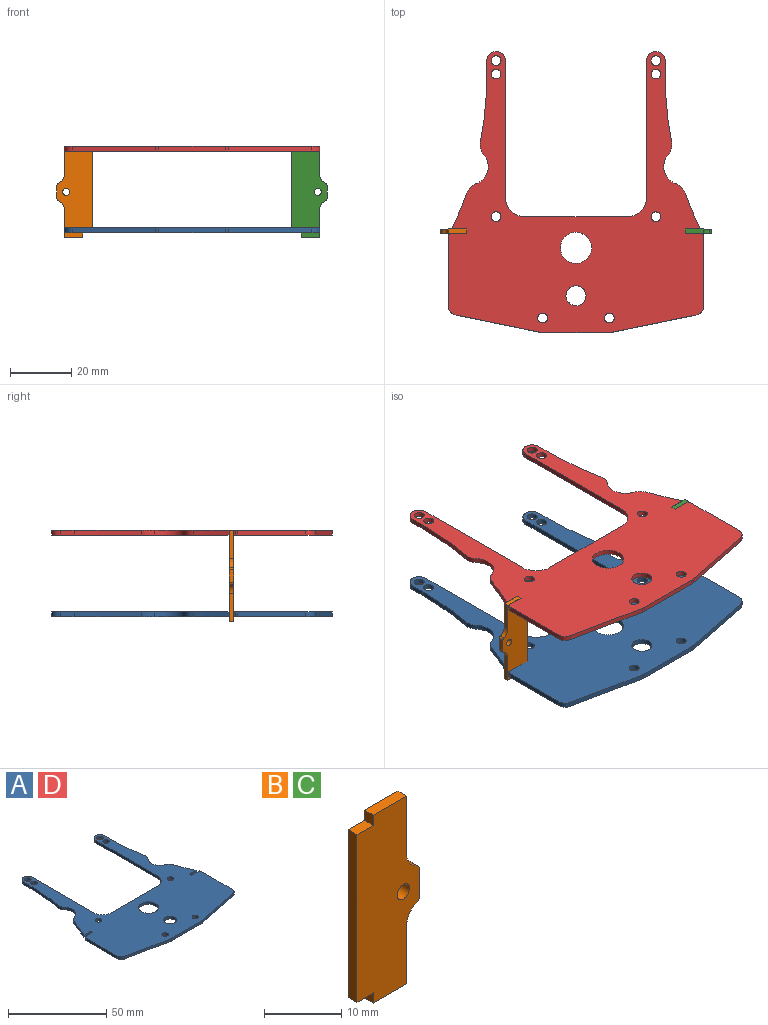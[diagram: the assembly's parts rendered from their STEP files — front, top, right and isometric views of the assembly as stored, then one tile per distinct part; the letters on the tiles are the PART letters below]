
ASSEMBLY  parts=4 mates=3
PART A: 55 faces, bbox 83.2x91.5x1.6 mm
  f0: cylinder r=116.85mm len=11.6mm, axis (0,0,-1), area 19.7mm2, adj f1,f6,f47,f52
  f1: plane 91.49x83.18mm, normal (0,0,-1), area 3595.5mm2, adj f0,f2,f3,f4,f5,f7,f8,f9
  f2: cylinder r=116.85mm len=1.57mm, axis (0,0,-1), area 0.7mm2, adj f1,f6,f20,f49
  f3: cylinder r=116.85mm len=1.57mm, axis (0,0,-1), area 0.7mm2, adj f1,f6,f10,f53
  f4: cylinder r=116.85mm len=22mm, axis (0,0,-1), area 34.7mm2, adj f1,f6,f9,f48
  f5: cylinder r=116.85mm len=22mm, axis (0,0,-1), area 34.7mm2, adj f1,f6,f22,f45
  f6: plane 91.49x83.18mm, normal (0,0,1), area 3595.5mm2, adj f0,f2,f3,f4,f5,f7,f8,f9
  f7: cylinder r=3mm len=6mm, axis (0,0,-1), area 14.8mm2, adj f1,f6,f8,f32
  f8: plane 4.35x1.57mm, normal (-1,0,0), area 6.8mm2, adj f1,f6,f7,f9
  f9: plane 1.57x0.09mm, normal (-1,0,0), area 0.1mm2, adj f1,f4,f6,f8
  f10: cylinder r=1.59mm len=1.57mm, axis (0,0,-1), area 1.2mm2, adj f1,f3,f6,f11
  f11: plane 22.2x1.57mm, normal (-1,0,0), area 34.9mm2, adj f1,f6,f10,f12
  f12: cylinder r=3.18mm len=3.11mm, axis (0,0,-1), area 6.8mm2, adj f1,f6,f11,f13
  f13: plane 27.26x5.56mm, normal (-0.2,-0.98,0), area 43.7mm2, adj f1,f6,f12,f14
  f14: cylinder r=4.68mm len=1.57mm, axis (0,0,-1), area 1.5mm2, adj f1,f6,f13,f15
  f15: plane 21.7x1.57mm, normal (0,-1,0), area 34.1mm2, adj f1,f6,f14,f16
  f16: cylinder r=4.68mm len=1.57mm, axis (0,0,-1), area 1.5mm2, adj f1,f6,f15,f17
  f17: plane 27.26x5.56mm, normal (0.2,-0.98,0), area 43.7mm2, adj f1,f6,f16,f18
  f18: cylinder r=3.18mm len=3.11mm, axis (0,0,-1), area 6.8mm2, adj f1,f6,f17,f19
  f19: plane 22.2x1.57mm, normal (1,0,0), area 34.9mm2, adj f1,f6,f18,f20
  f20: cylinder r=1.59mm len=1.57mm, axis (0,0,-1), area 1.2mm2, adj f1,f2,f6,f19
  f21: cylinder r=116.85mm len=11.6mm, axis (0,0,-1), area 19.7mm2, adj f1,f6,f46,f50
  f22: plane 1.57x0.09mm, normal (1,0,0), area 0.1mm2, adj f1,f5,f6,f23
  f23: plane 4.35x1.57mm, normal (1,0,0), area 6.8mm2, adj f1,f6,f22,f24
  f24: cylinder r=3mm len=6mm, axis (0,0,-1), area 14.8mm2, adj f1,f6,f23,f25
  f25: plane 4.34x1.57mm, normal (-1,0,0), area 6.8mm2, adj f1,f6,f24,f26
  f26: plane 40.11x1.57mm, normal (-1,0,0), area 63mm2, adj f1,f6,f25,f27
  f27: cylinder r=6.35mm len=6.35mm, axis (0,0,-1), area 15.7mm2, adj f1,f6,f26,f28
  f28: plane 16.67x1.57mm, normal (0,1,0), area 26.2mm2, adj f1,f6,f27,f29
  f29: plane 16.67x1.57mm, normal (0,1,0), area 26.2mm2, adj f1,f6,f28,f30
  f30: cylinder r=6.35mm len=6.35mm, axis (0,0,-1), area 15.7mm2, adj f1,f6,f29,f31
  f31: plane 40.11x1.57mm, normal (1,0,0), area 63mm2, adj f1,f6,f30,f32
  f32: plane 4.34x1.57mm, normal (1,0,0), area 6.8mm2, adj f1,f6,f7,f31
  f33: cylinder r=1.6mm len=3.2mm, axis (0,0,-1), area 15.8mm2, adj f1,f6
  f34: cylinder r=1.6mm len=3.2mm, axis (0,0,-1), area 15.8mm2, adj f1,f6
  f35: cylinder r=1.6mm len=3.2mm, axis (0,0,-1), area 15.8mm2, adj f1,f6
  f36: cylinder r=1.6mm len=3.2mm, axis (0,0,-1), area 15.8mm2, adj f1,f6
  f37: cylinder r=1.6mm len=3.2mm, axis (0,0,-1), area 15.8mm2, adj f1,f6
  f38: cylinder r=1.6mm len=3.2mm, axis (0,0,-1), area 15.8mm2, adj f1,f6
  f39: cylinder r=1.6mm len=3.2mm, axis (0,0,-1), area 15.8mm2, adj f1,f6
  f40: cylinder r=1.6mm len=3.2mm, axis (0,0,-1), area 15.8mm2, adj f1,f6
  f41: cylinder r=3.26mm len=6.53mm, axis (0,0,-1), area 32.2mm2, adj f1,f6
  f42: cylinder r=5.08mm len=10.16mm, axis (0,0,-1), area 50.1mm2, adj f1,f6
  f43: cylinder r=6mm len=9.54mm, axis (0,0,1), area 18.2mm2, adj f1,f6,f47,f48
  f44: cylinder r=6mm len=9.54mm, axis (0,0,1), area 18.2mm2, adj f1,f6,f45,f46
  f45: cylinder r=5mm len=4.18mm, axis (0,0,-1), area 7mm2, adj f1,f5,f6,f44
  f46: cylinder r=5mm len=3.06mm, axis (0,0,1), area 7mm2, adj f1,f6,f21,f44
  f47: cylinder r=5mm len=3.06mm, axis (0,0,1), area 7mm2, adj f0,f1,f6,f43
  f48: cylinder r=5mm len=4.18mm, axis (0,0,-1), area 7mm2, adj f1,f4,f6,f43
  f49: plane 5.71x1.57mm, normal (0,1,0), area 9mm2, adj f1,f2,f6,f51
  f50: plane 4.93x1.57mm, normal (0,-1,0), area 7.7mm2, adj f1,f6,f21,f51
  f51: plane 1.6x1.57mm, normal (1,0,0), area 2.5mm2, adj f1,f6,f49,f50
  f52: plane 4.93x1.57mm, normal (0,-1,0), area 7.7mm2, adj f0,f1,f6,f54
  f53: plane 5.71x1.57mm, normal (0,1,0), area 9mm2, adj f1,f3,f6,f54
  f54: plane 1.6x1.57mm, normal (-1,0,0), area 2.5mm2, adj f1,f6,f52,f53
PART B: 17 faces, bbox 11.5x1.6x29.8 mm
  f0: plane 6.09x1.6mm, normal (0,0,1), area 9.7mm2, adj f3,f4,f8,f16
  f1: plane 6.09x1.6mm, normal (0,0,-1), area 9.7mm2, adj f3,f4,f6,f13
  f2: plane 26.6x1.6mm, normal (-1,0,0), area 42.6mm2, adj f3,f4,f14,f15
  f3: plane 29.8x11.5mm, normal (0,-1,0), area 273.6mm2, adj f0,f1,f2,f5,f6,f7,f8,f9
  f4: plane 29.8x11.5mm, normal (0,1,0), area 273.6mm2, adj f0,f1,f2,f5,f6,f7,f8,f9
  f5: cylinder r=1.15mm len=2.3mm, axis (0,-1,0), area 11.6mm2, adj f3,f4
  f6: plane 9.23x1.6mm, normal (1,0,0), area 14.8mm2, adj f1,f3,f4,f11
  f7: plane 4x1.6mm, normal (1,0,0), area 6.4mm2, adj f3,f4,f9,f10
  f8: plane 9.23x1.6mm, normal (1,0,0), area 14.8mm2, adj f0,f3,f4,f12
  f9: cylinder r=1mm len=1.6mm, axis (0,1,0), area 1.9mm2, adj f3,f4,f7,f11
  f10: cylinder r=1mm len=1.6mm, axis (0,1,0), area 1.9mm2, adj f3,f4,f7,f12
  f11: cylinder r=3mm len=2.75mm, axis (0,1,0), area 5.6mm2, adj f3,f4,f6,f9
  f12: cylinder r=3mm len=2.75mm, axis (0,1,0), area 5.6mm2, adj f3,f4,f8,f10
  f13: plane 1.6x1.6mm, normal (-1,0,0), area 2.6mm2, adj f1,f3,f4,f14
  f14: plane 3x1.6mm, normal (0,0,-1), area 4.8mm2, adj f2,f3,f4,f13
  f15: plane 3x1.6mm, normal (0,0,1), area 4.8mm2, adj f2,f3,f4,f16
  f16: plane 1.6x1.6mm, normal (-1,0,0), area 2.6mm2, adj f0,f3,f4,f15
PART C: same geometry as B
PART D: same geometry as A
PLACE A t=(-41.59,-28.67,-1.57)mm fixed
PLACE B rot(axis=(0,0,1),180deg) t=(-37.5,3.42,11.67)mm
PLACE C t=(37.5,5.02,11.67)mm
PLACE D t=(-41.59,-28.67,25)mm
MATE fastened D.f6 <-> C.f0  axis (0,0,1) through (35.5,5.02,26.57)mm
MATE fastened A.f38 <-> D.f38  axis (0,0,1) through (26.02,9.02,0)mm
MATE fastened B.f5 <-> C.f3  axis (0,-1,0) through (-41,3.42,11.67)mm
